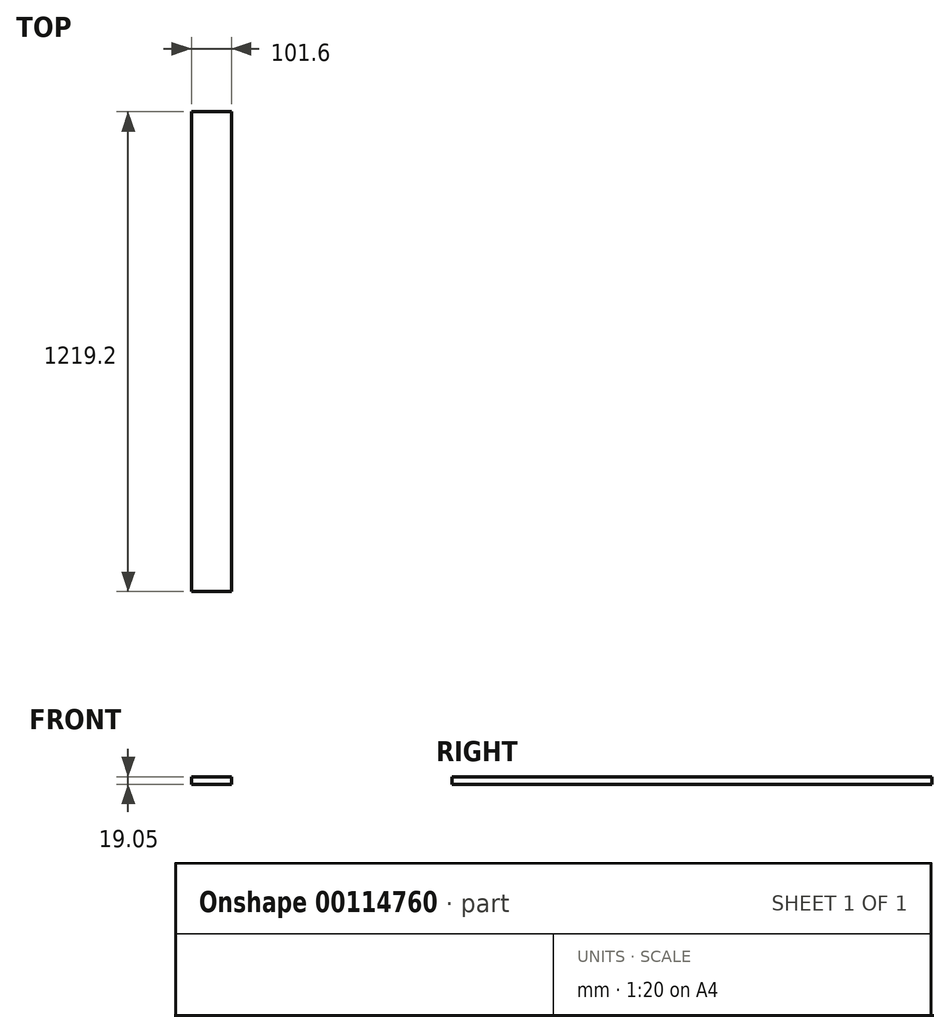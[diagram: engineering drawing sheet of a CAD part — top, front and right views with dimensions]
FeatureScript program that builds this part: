
annotation { "Feature Type Name" : "Feature", "Feature Type Description" : "" }
export const myFeature = defineFeature(function(context is Context, id is Id, definition is map)
    precondition{}
    {
        {
            var Q0;
            Q0=qCreatedBy(makeId("Top.planeOp"),FACE);
            var sketch = newSketch(context, id + "F0", { "sketchPlane" : qUnion([Q0])});
            skLineSegment(sketch, "E0.bottom", {"start": v(0, 0) * mm, "end": v(101.6, 0) * mm});
            skLineSegment(sketch, "E0.top", {"start": v(0, 1219.2) * mm, "end": v(101.6, 1219.2) * mm});
            skLineSegment(sketch, "E0.left", {"start": v(0, 0) * mm, "end": v(0, 1219.2) * mm});
            skLineSegment(sketch, "E0.right", {"start": v(101.6, 0) * mm, "end": v(101.6, 1219.2) * mm});
            skSolve(sketch);
        }
        {
            var Q0;
            Q0=qSketchRegion(id+"F0",true);
            extrude(context, id + "F1", {"entities" : qUnion([Q0]), "depth" : 19.05 * mm});
        }
    });
